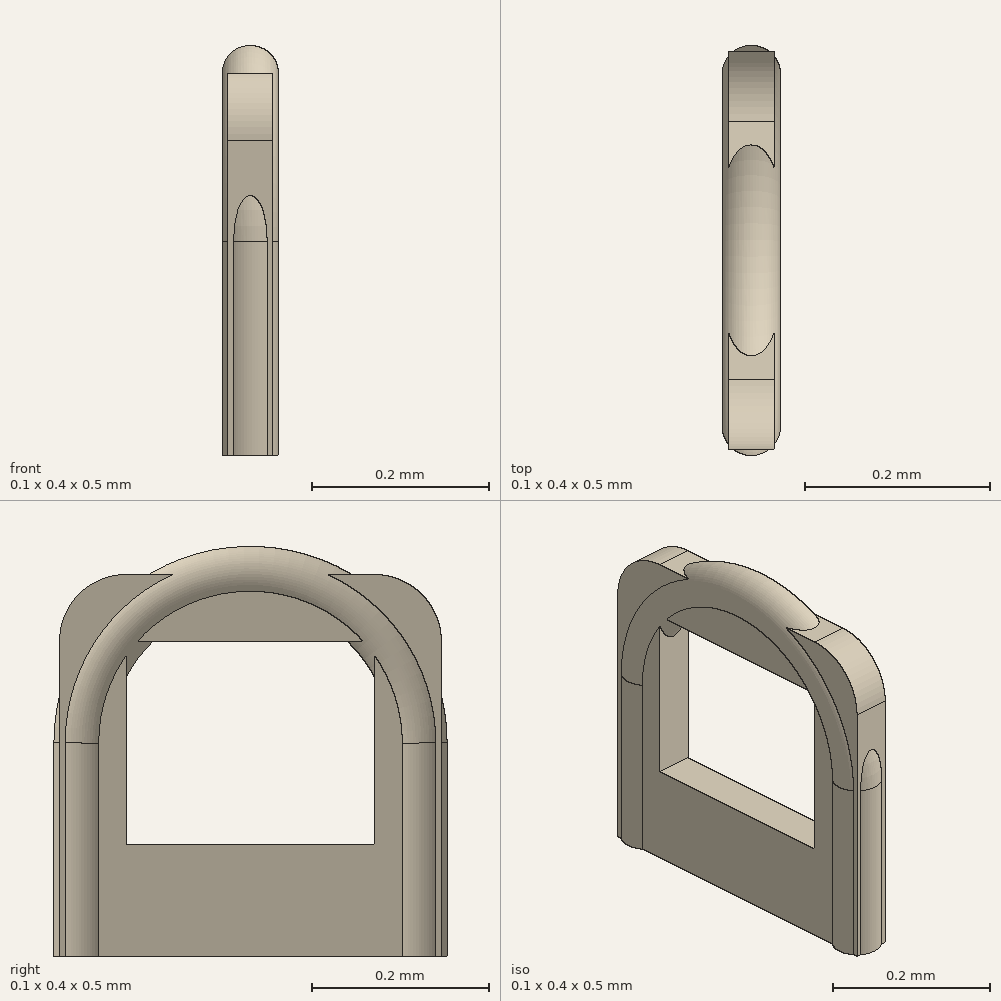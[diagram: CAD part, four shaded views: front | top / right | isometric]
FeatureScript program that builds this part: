
annotation { "Feature Type Name" : "Feature", "Feature Type Description" : "" }
export const myFeature = defineFeature(function(context is Context, id is Id, definition is map)
    precondition{}
    {
        {
            var Q0;
            Q0=qCreatedBy(makeId("Right.planeOp"),FACE);
            var sketch = newSketch(context, id + "F0", { "sketchPlane" : qUnion([Q0])});
            skLineSegment(sketch, "E0", {"start": v(-0.2, 0) * mm, "end": v(-0.2, 0.24) * mm});
            skLineSegment(sketch, "E1", {"start": v(0, 0) * mm, "end": v(0, 0.43) * mm, "construction": true});
            skLineSegment(sketch, "E2.MirrorCS", {"start": v(0.2, 0) * mm, "end": v(0.2, 0.24) * mm});
            skArc(sketch, "E3", {"start": v(-0.2, 0.24) * mm, "mid": v(0, 0.43) * mm, "end": v(0.2, 0.24) * mm});
            skSolve(sketch);
        }
        {
            var Q0;
            Q0=qCreatedBy(makeId("Top.planeOp"),FACE);
            var sketch = newSketch(context, id + "F1", { "sketchPlane" : qUnion([Q0])});
            skCircle(sketch, "E4", {"center": v(0, -0.2) * mm, "radius": 0.03 * mm});
            skSolve(sketch);
        }
        {
            var Q0;
            Q0=makeQuery(id+"F1.imprint","IMPRINT",FACE,{"disambiguationData":[TD([[makeQuery(id+"F1.imprint","IMPRINT",EDGE,{"derivedFrom":sQuery(id+"F1.wireOp",EDGE,"E4")}),1.0]])]});
            var Q1;
            Q1=sQuery(id+"F0.wireOp",EDGE,"E0");
            var Q2;
            Q2=sQuery(id+"F0.wireOp",EDGE,"E3");
            var Q3;
            Q3=sQuery(id+"F0.wireOp",EDGE,"E2.MirrorCS");
            sweep(context, id + "F2", {"profiles" : qUnion([Q0]), "path" : qUnion([Q1, Q2, Q3])});
        }
        {
            var Q0;
            Q0=qCreatedBy(makeId("Right.planeOp"),FACE);
            var sketch = newSketch(context, id + "F3", { "sketchPlane" : qUnion([Q0])});
            skLineSegment(sketch, "E5", {"start": v(-0.22, 0) * mm, "end": v(0.22, 0) * mm});
            skLineSegment(sketch, "E6", {"start": v(-0.14, 0.43) * mm, "end": v(0.14, 0.43) * mm});
            skPoint(sketch, "E7", {"position": v(0, 0.43) * mm});
            skLineSegment(sketch, "E8", {"start": v(-0.22, 0) * mm, "end": v(-0.22, 0.36) * mm});
            skArc(sketch, "E9", {"start": v(-0.14, 0.43) * mm, "mid": v(-0.2, 0.4) * mm, "end": v(-0.22, 0.36) * mm});
            skLineSegment(sketch, "E10", {"start": v(0, 0) * mm, "end": v(0, 0.43) * mm, "construction": true});
            skArc(sketch, "E11.MirrorCS", {"start": v(0.14, 0.43) * mm, "mid": v(0.2, 0.4) * mm, "end": v(0.22, 0.36) * mm});
            skLineSegment(sketch, "E12.MirrorCS", {"start": v(0.22, 0) * mm, "end": v(0.22, 0.36) * mm});
            skLineSegment(sketch, "E13", {"start": v(-0.14, 0.36) * mm, "end": v(0.14, 0.36) * mm});
            skLineSegment(sketch, "E14", {"start": v(0.14, 0.36) * mm, "end": v(0.14, 0.13) * mm});
            skLineSegment(sketch, "E15", {"start": v(0.14, 0.13) * mm, "end": v(-0.14, 0.13) * mm});
            skLineSegment(sketch, "E16", {"start": v(-0.14, 0.13) * mm, "end": v(-0.14, 0.36) * mm});
            skSolve(sketch);
        }
        {
            var Q0;
            Q0=makeQuery(id+"F3.imprint","IMPRINT",FACE,{"disambiguationData":[TD([[makeQuery(id+"F3.imprint","IMPRINT",EDGE,{"derivedFrom":sQuery(id+"F3.wireOp",EDGE,"E5")}),1.0]])]});
            extrude(context, id + "F4", {"entities" : qUnion([Q0]), "endBound" : BoundingType.SYMMETRIC, "depth" : 0.05 * mm});
        }
    });
